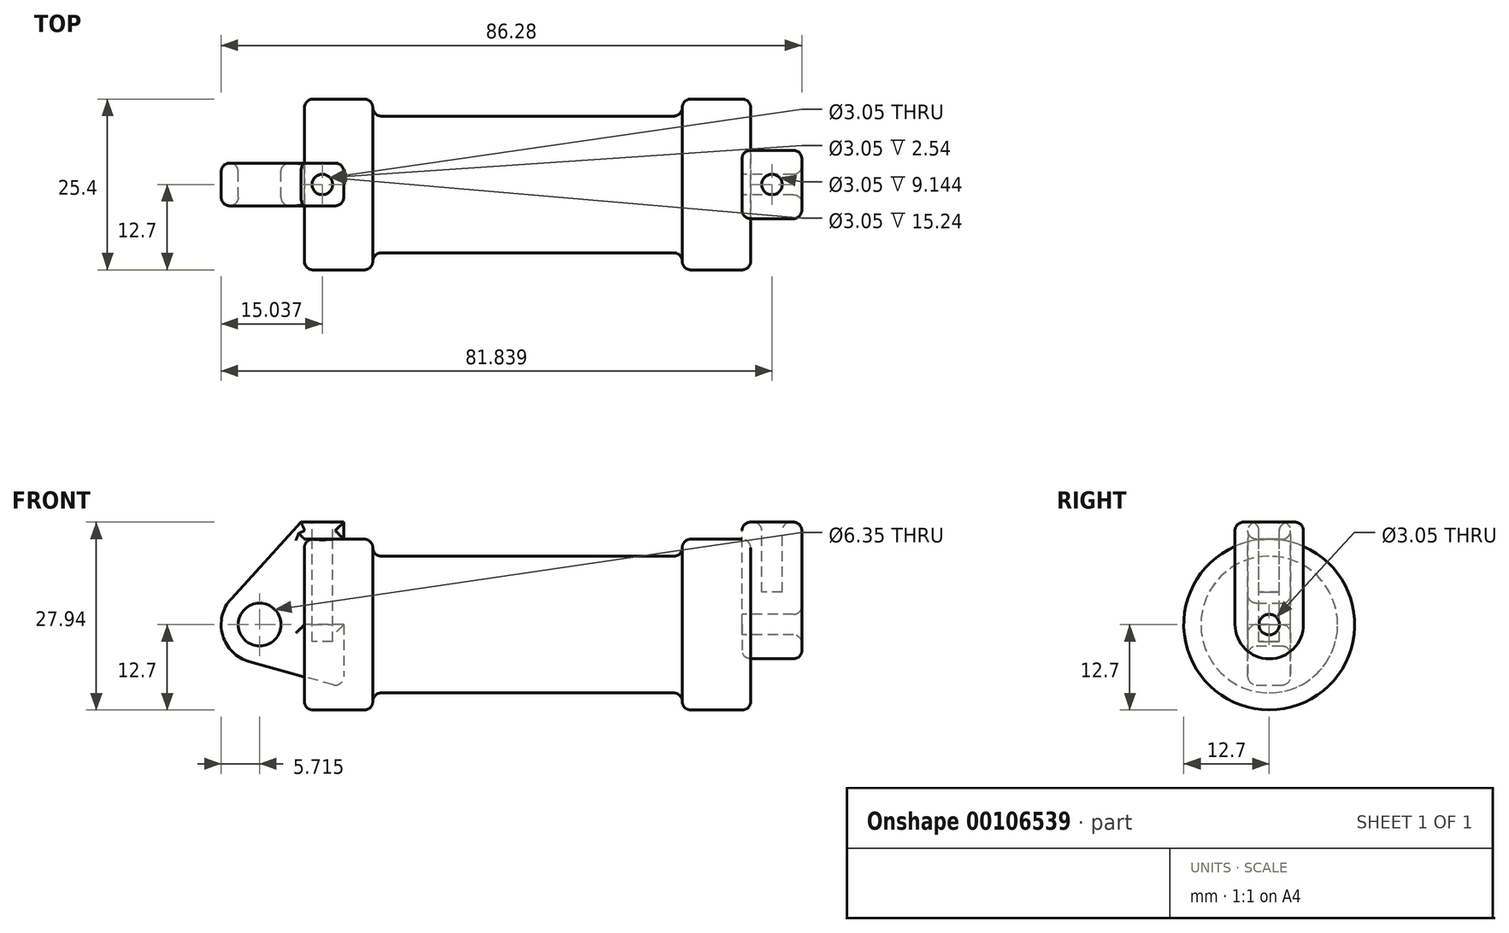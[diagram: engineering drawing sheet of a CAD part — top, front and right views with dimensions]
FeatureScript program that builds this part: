
annotation { "Feature Type Name" : "Feature", "Feature Type Description" : "" }
export const myFeature = defineFeature(function(context is Context, id is Id, definition is map)
    precondition{}
    {
        {
            var Q0;
            Q0=qCreatedBy(makeId("Front.planeOp"),FACE);
            var sketch = newSketch(context, id + "F0", { "sketchPlane" : qUnion([Q0])});
            skLineSegment(sketch, "E0", {"start": v(0, 0) * mm, "end": v(0, 12.7) * mm});
            skLineSegment(sketch, "E1", {"start": v(0, 12.7) * mm, "end": v(10.16, 12.7) * mm});
            skLineSegment(sketch, "E2", {"start": v(10.16, 12.7) * mm, "end": v(10.16, 10.16) * mm});
            skLineSegment(sketch, "E3", {"start": v(10.16, 10.16) * mm, "end": v(56.13, 10.16) * mm});
            skLineSegment(sketch, "E4", {"start": v(56.13, 10.16) * mm, "end": v(56.13, 12.7) * mm});
            skLineSegment(sketch, "E5", {"start": v(56.13, 12.7) * mm, "end": v(66.3, 12.7) * mm});
            skLineSegment(sketch, "E6", {"start": v(66.3, 12.7) * mm, "end": v(66.3, 0) * mm});
            skLineSegment(sketch, "E7", {"start": v(66.3, 0) * mm, "end": v(0, 0) * mm});
            skLineSegment(sketch, "E8", {"start": v(5.84, 15.24) * mm, "end": v(-0.5, 15.24) * mm});
            skLineSegment(sketch, "E9", {"start": v(-0.5, 15.24) * mm, "end": v(-10.88, 3.85) * mm});
            skLineSegment(sketch, "E10", {"start": v(0, 0) * mm, "end": v(-6.65, 0) * mm});
            skCircle(sketch, "E11", {"center": v(-6.65, 0) * mm, "radius": 5.72 * mm});
            skCircle(sketch, "E12", {"center": v(-6.65, 0) * mm, "radius": 3.18 * mm});
            skLineSegment(sketch, "E13", {"start": v(5.84, 15.24) * mm, "end": v(5.84, -9.4) * mm});
            skLineSegment(sketch, "E14", {"start": v(5.84, -9.4) * mm, "end": v(-8.18, -5.5) * mm});
            skSolve(sketch);
        }
        {
            var Q0;
            {var subQ0=sQuery(id+"F0.wireOp",EDGE,"E2");Q0=makeQuery(id+"F0.imprint","IMPRINT",FACE,{"disambiguationData":[TD([[makeQuery(id+"F0.imprint","IMPRINT",EDGE,{"derivedFrom":subQ0}),-1.0]])]});}
            var Q1;
            {var subQ0=sQuery(id+"F0.wireOp",EDGE,"E0");Q1=makeQuery(id+"F0.imprint","IMPRINT",FACE,{"disambiguationData":[TD([[makeQuery(id+"F0.imprint","IMPRINT",EDGE,{"derivedFrom":subQ0}),-1.0]])]});}
            var Q2;
            Q2=sQuery(id+"F0.wireOp",EDGE,"E7");
            revolve(context, id + "F1", {"entities" : qUnion([Q0, Q1]), "axis" : qUnion([Q2]), "revolveType" : RevolveType.FULL});
        }
        {
            var Q0;
            {var subQ0=sQuery(id+"F0.wireOp",EDGE,"E14");Q0=makeQuery(id+"F0.imprint","IMPRINT",FACE,{"disambiguationData":[TD([[makeQuery(id+"F0.imprint","IMPRINT",EDGE,{"derivedFrom":subQ0}),-1.0]])]});}
            var Q1;
            {var subQ3=sQuery(id+"F0.wireOp",EDGE,"E0");Q1=makeQuery(id+"F0.imprint","IMPRINT",FACE,{"disambiguationData":[TD([[makeQuery(id+"F0.imprint","IMPRINT",EDGE,{"derivedFrom":subQ3}),1.0]])]});}
            var Q2;
            {var subQ4=sQuery(id+"F0.wireOp",EDGE,"E12");Q2=makeQuery(id+"F0.imprint","IMPRINT",FACE,{"disambiguationData":[TD([[makeQuery(id+"F0.imprint","IMPRINT",EDGE,{"derivedFrom":subQ4}),-1.0]])]});}
            extrude(context, id + "F2", {"entities" : qUnion([Q0, Q1, Q2]), "endBound" : BoundingType.SYMMETRIC, "depth" : 6.35 * mm});
        }
        {
            var Q0;
            Q0=makeQuery(id+"F1.opRevolve","SWEPT_FACE",FACE,{"disambiguationData":[OSD([sQuery(id+"F0.wireOp",EDGE,"E6")])]});
            var sketch = newSketch(context, id + "F3", { "sketchPlane" : qUnion([Q0])});
            skCircle(sketch, "E15", {"center": v(0, 0) * mm, "radius": 1.52 * mm});
            skCircle(sketch, "E16", {"center": v(0, 0) * mm, "radius": 5.08 * mm});
            skLineSegment(sketch, "E17", {"start": v(5.08, 0) * mm, "end": v(5.08, 15.24) * mm});
            skLineSegment(sketch, "E18", {"start": v(-5.08, 0) * mm, "end": v(-5.08, 15.24) * mm});
            skLineSegment(sketch, "E19", {"start": v(-5.08, 15.24) * mm, "end": v(5.08, 15.24) * mm});
            skSolve(sketch);
        }
        {
            var Q0;
            Q0 = qSketchRegion(id + "F3", true);
            extrude(context, id + "F4", {"entities" : qUnion([Q0]), "depth" : 7.62 * mm, "hasSecondDirection" : true, "secondDirectionOppositeDirection" : true, "secondDirectionDepth" : 1.27 * mm});
        }
        {
            var Q0;
            Q0=makeQuery(id+"F2.opExtrude","SWEPT_FACE",FACE,{"disambiguationData":[OSD([sQuery(id+"F0.wireOp",EDGE,"E8")])]});
            var sketch = newSketch(context, id + "F5", { "sketchPlane" : qUnion([Q0])});
            skCircle(sketch, "E20", {"center": v(2.67, 0) * mm, "radius": 1.52 * mm});
            skPoint(sketch, "E20.centerSnap0", {"position": v(2.67, -3.18) * mm});
            skPoint(sketch, "E20.centerSnap1", {"position": v(5.84, 0) * mm});
            skSolve(sketch);
        }
        {
            var Q0;
            Q0=makeQuery(id+"F5.imprint","IMPRINT",FACE,{"disambiguationData":[TD([[makeQuery(id+"F5.imprint","IMPRINT",EDGE,{"derivedFrom":sQuery(id+"F5.wireOp",EDGE,"E20")}),1.0]])]});
            extrude(context, id + "F6", {"entities" : qUnion([Q0]), "operationType" : NewBodyOperationType.REMOVE, "oppositeDirection" : true, "depth" : 17.78 * mm});
        }
        {
            var Q0;
            Q0=makeQuery(id+"F4.opExtrude","SWEPT_FACE",FACE,{"disambiguationData":[OSD([sQuery(id+"F3.wireOp",EDGE,"E19")])]});
            var sketch = newSketch(context, id + "F7", { "sketchPlane" : qUnion([Q0])});
            skCircle(sketch, "E21", {"center": v(69.47, 0) * mm, "radius": 1.52 * mm});
            skPoint(sketch, "E21.centerSnap0", {"position": v(69.47, 5.08) * mm});
            skPoint(sketch, "E21.centerSnap1", {"position": v(65.02, 0) * mm});
            skSolve(sketch);
        }
        {
            var Q0;
            Q0=makeQuery(id+"F7.imprint","IMPRINT",FACE,{"disambiguationData":[TD([[makeQuery(id+"F7.imprint","IMPRINT",EDGE,{"derivedFrom":sQuery(id+"F7.wireOp",EDGE,"E21")}),1.0]])]});
            extrude(context, id + "F8", {"entities" : qUnion([Q0]), "operationType" : NewBodyOperationType.REMOVE, "oppositeDirection" : true, "depth" : 10.4 * mm});
        }
        {
            var Q0;
            Q0=makeQuery(id+"F1.opRevolve","SWEPT_EDGE",EDGE,{"disambiguationData":[OSD([sQuery(id+"F0.wireOp",EDGE,"E1"),sQuery(id+"F0.wireOp",EDGE,"E2")])]});
            var Q1;
            Q1=makeQuery(id+"F1.opRevolve","SWEPT_FACE",FACE,{"disambiguationData":[OSD([sQuery(id+"F0.wireOp",EDGE,"E6")])]});
            var Q2;
            Q2=makeQuery(id+"F1.opRevolve","SWEPT_FACE",FACE,{"disambiguationData":[OSD([sQuery(id+"F0.wireOp",EDGE,"E0")])]});
            var Q3;
            Q3=makeQuery(id+"F1.opRevolve","SWEPT_FACE",FACE,{"disambiguationData":[OSD([sQuery(id+"F0.wireOp",EDGE,"E4")])]});
            var Q4;
            Q4=makeQuery(id+"F1.opRevolve","SWEPT_FACE",FACE,{"disambiguationData":[OSD([sQuery(id+"F0.wireOp",EDGE,"E2")])]});
            fillet(context, id + "F9", {"entities" : qUnion([Q0, Q1, Q2, Q3, Q4]), "radius" : 1.27 * mm, "tangentPropagation" : true, "allowEdgeOverflow" : false});
        }
        {
            var Q0;
            Q0=makeQuery(id+"F2.opExtrude","CAP_FACE",FACE,{"disambiguationData":[OSD([sQuery(id+"F0.wireOp",EDGE,"E0"),sQuery(id+"F0.wireOp",EDGE,"E1"),sQuery(id+"F0.wireOp",EDGE,"E7"),sQuery(id+"F0.wireOp",EDGE,"E8"),sQuery(id+"F0.wireOp",EDGE,"E9"),sQuery(id+"F0.wireOp",EDGE,"E11"),sQuery(id+"F0.wireOp",EDGE,"E12"),sQuery(id+"F0.wireOp",EDGE,"E13"),sQuery(id+"F0.wireOp",EDGE,"E14")])],"isStart":false});
            var Q1;
            Q1=makeQuery(id+"F2.opExtrude","SWEPT_FACE",FACE,{"disambiguationData":[OSD([sQuery(id+"F0.wireOp",EDGE,"E11")])]});
            var Q2;
            Q2=makeQuery(id+"F2.opExtrude","CAP_FACE",FACE,{"disambiguationData":[OSD([sQuery(id+"F0.wireOp",EDGE,"E0"),sQuery(id+"F0.wireOp",EDGE,"E1"),sQuery(id+"F0.wireOp",EDGE,"E7"),sQuery(id+"F0.wireOp",EDGE,"E8"),sQuery(id+"F0.wireOp",EDGE,"E9"),sQuery(id+"F0.wireOp",EDGE,"E11"),sQuery(id+"F0.wireOp",EDGE,"E12"),sQuery(id+"F0.wireOp",EDGE,"E13"),sQuery(id+"F0.wireOp",EDGE,"E14")])],"isStart":true});
            var Q3;
            Q3=makeQuery(id+"F4.opExtrude","CAP_FACE",FACE,{"disambiguationData":[OSD([sQuery(id+"F3.wireOp",EDGE,"E15"),sQuery(id+"F3.wireOp",EDGE,"E16"),sQuery(id+"F3.wireOp",EDGE,"E17"),sQuery(id+"F3.wireOp",EDGE,"E18"),sQuery(id+"F3.wireOp",EDGE,"E19")])],"isStart":false});
            var Q4;
            Q4=makeQuery(id+"F4.opExtrude","SWEPT_FACE",FACE,{"disambiguationData":[OSD([sQuery(id+"F3.wireOp",EDGE,"E16")])]});
            var Q5;
            Q5=makeQuery(id+"F4.opExtrude","SWEPT_FACE",FACE,{"disambiguationData":[OSD([sQuery(id+"F3.wireOp",EDGE,"E18")])]});
            var Q6;
            Q6=makeQuery(id+"F4.opExtrude","SWEPT_FACE",FACE,{"disambiguationData":[OSD([sQuery(id+"F3.wireOp",EDGE,"E19")])]});
            var Q7;
            Q7=makeQuery(id+"F4.opExtrude","SWEPT_FACE",FACE,{"disambiguationData":[OSD([sQuery(id+"F3.wireOp",EDGE,"E17")])]});
            var Q8;
            Q8=makeQuery(id+"F2.opExtrude","SWEPT_FACE",FACE,{"disambiguationData":[OSD([sQuery(id+"F0.wireOp",EDGE,"E14")])]});
            fillet(context, id + "F10", {"entities" : qUnion([Q0, Q1, Q2, Q3, Q4, Q5, Q6, Q7, Q8]), "radius" : 1.27 * mm, "tangentPropagation" : true, "allowEdgeOverflow" : false});
        }
    });
